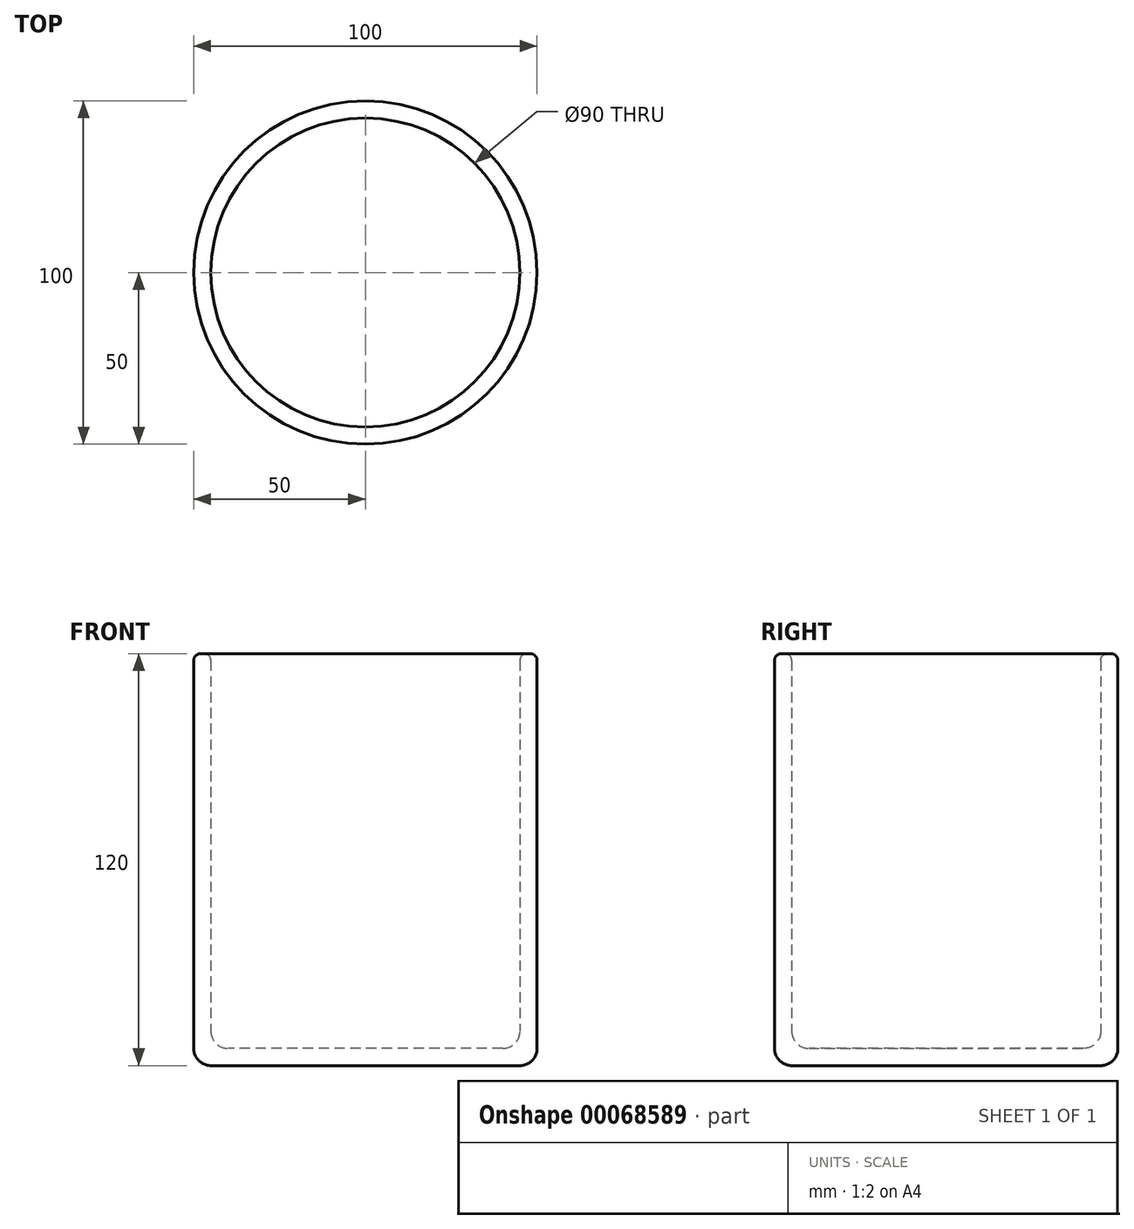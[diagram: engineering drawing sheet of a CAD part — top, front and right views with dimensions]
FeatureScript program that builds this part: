
annotation { "Feature Type Name" : "Feature", "Feature Type Description" : "" }
export const myFeature = defineFeature(function(context is Context, id is Id, definition is map)
    precondition{}
    {
        {
            var Q0;
            Q0=qCreatedBy(makeId("Top.planeOp"),FACE);
            var sketch = newSketch(context, id + "F0", { "sketchPlane" : qUnion([Q0])});
            skCircle(sketch, "E0", {"center": v(0, 0) * mm, "radius": 50 * mm});
            skSolve(sketch);
        }
        {
            var Q0;
            Q0 = qSketchRegion(id + "F0", true);
            extrude(context, id + "F1", {"entities" : qUnion([Q0]), "depth" : 120 * mm});
        }
        {
            var Q0;
            Q0=makeQuery(id+"F1.opExtrude","CAP_FACE",FACE,{"disambiguationData":[OSD([sQuery(id+"F0.wireOp",EDGE,"E0")])],"isStart":false});
            shell(context, id + "F2", {"entities" : qUnion([Q0]), "thickness" : 5 * mm});
        }
        {
            var Q0;
            {var subQ0=sQuery(id+"F0.wireOp",EDGE,"E0");Q0=makeQuery(id+"F2.opShell","OFFSET_EDGE",EDGE,{"disambiguationData":[OSD([subQ0]),TDD([makeQuery(id+"F1.opExtrude","CAP_EDGE",EDGE,{"disambiguationData":[OSD([subQ0])],"isStart":true})])]});}
            var Q1;
            Q1=makeQuery(id+"F1.opExtrude","CAP_EDGE",EDGE,{"disambiguationData":[OSD([sQuery(id+"F0.wireOp",EDGE,"E0")])],"isStart":true});
            fillet(context, id + "F3", {"entities" : qUnion([Q0, Q1]), "radius" : 5 * mm, "tangentPropagation" : true, "allowEdgeOverflow" : false});
        }
        {
            var Q0;
            {var subQ0=sQuery(id+"F0.wireOp",EDGE,"E0");Q0=makeQuery(id+"F2.opShell","OFFSET_EDGE",EDGE,{"disambiguationData":[OSD([subQ0]),TDD([makeQuery(id+"F1.opExtrude","CAP_EDGE",EDGE,{"disambiguationData":[OSD([subQ0])],"isStart":false})])]});}
            var Q1;
            Q1=makeQuery(id+"F1.opExtrude","CAP_EDGE",EDGE,{"disambiguationData":[OSD([sQuery(id+"F0.wireOp",EDGE,"E0")])],"isStart":false});
            fillet(context, id + "F4", {"entities" : qUnion([Q0, Q1]), "radius" : 2 * mm, "tangentPropagation" : true, "allowEdgeOverflow" : false});
        }
        {
            var Q0;
            Q0=qCreatedBy(makeId("Front.planeOp"),FACE);
            var sketch = newSketch(context, id + "F5", { "sketchPlane" : qUnion([Q0])});
            skFitSpline(sketch, "E1", {"points": [v(-47.3, 58.67) * mm, v(-60.55, 53.02) * mm, v(-72.58, 56.46) * mm, v(-74.54, 72.66) * mm, v(-77.98, 100.14) * mm, v(-65.22, 111.19) * mm, v(-47.3, 107.02) * mm], "startDerivative": vector(-82.54, -49.65) * mm, "endDerivative": vector(105.24, -44.83) * mm});
            skSolve(sketch);
        }
        {
            var Q0;
            Q0=qCreatedBy(makeId("Right.planeOp"),FACE);
            cPlane(context, id + "F6", {"entities" : qUnion([Q0]), "cplaneType" : CPlaneType.OFFSET, "offset" : 47.3 * mm, "oppositeDirection" : true, "width" : 150 * mm, "height" : 150 * mm});
        }
        {
            var Q0;
            Q0=qCreatedBy(id+"F6.planeOp",FACE);
            var sketch = newSketch(context, id + "F7", { "sketchPlane" : qUnion([Q0])});
            skCircle(sketch, "E2", {"center": v(0, 58.78) * mm, "radius": 2.7 * mm});
            skSolve(sketch);
        }
    });
